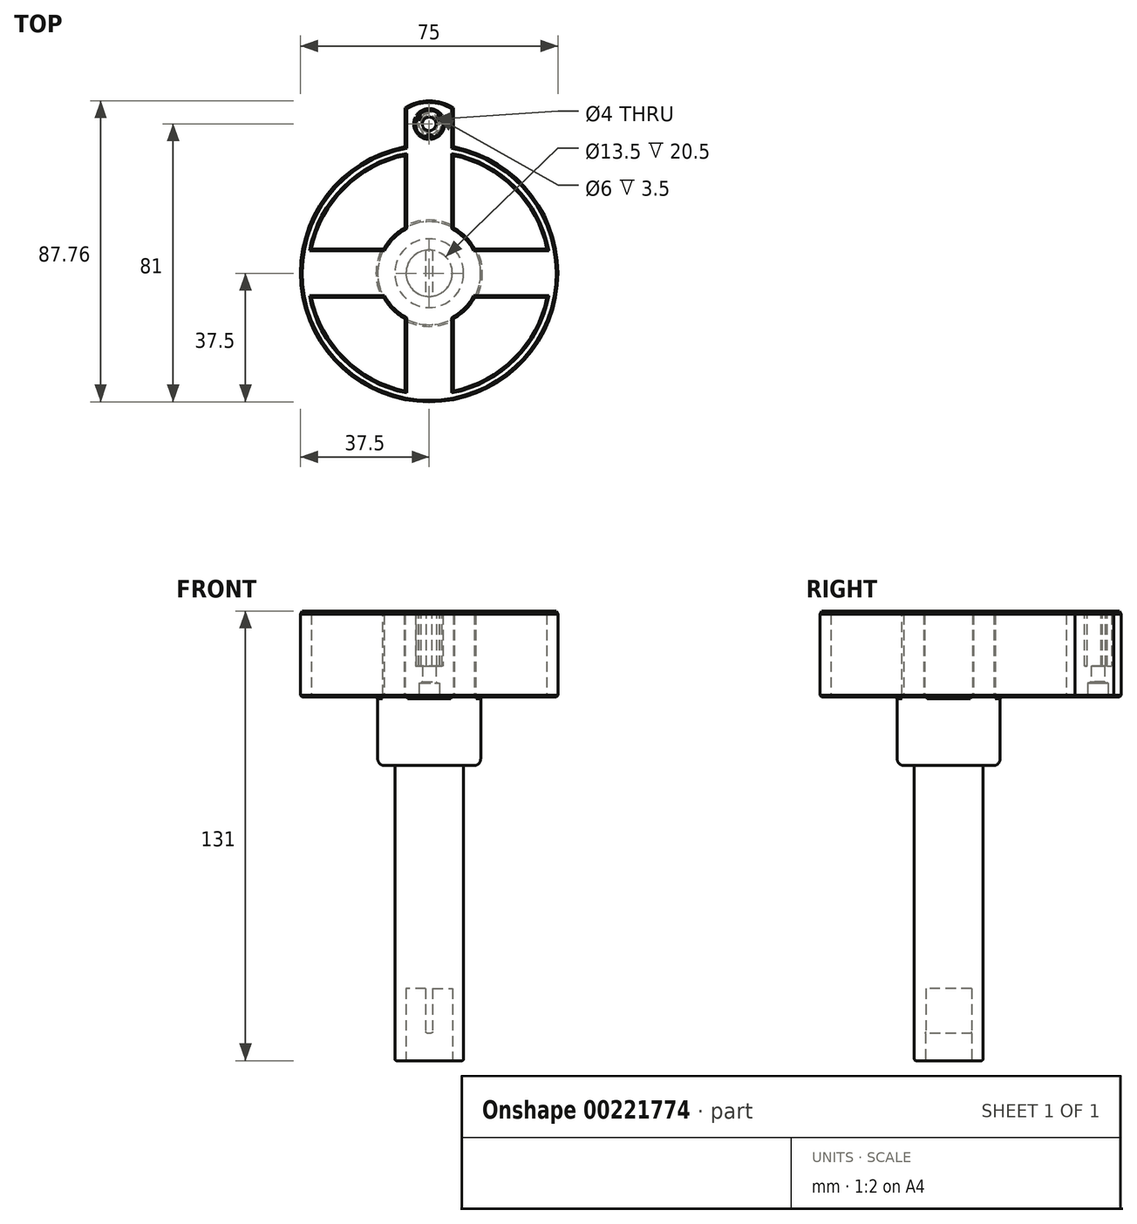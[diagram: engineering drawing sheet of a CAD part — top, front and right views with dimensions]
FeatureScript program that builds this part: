
annotation { "Feature Type Name" : "Feature", "Feature Type Description" : "" }
export const myFeature = defineFeature(function(context is Context, id is Id, definition is map)
    precondition{}
    {
        {
            var Q0;
            Q0=qCreatedBy(makeId("Top.planeOp"),FACE);
            var sketch = newSketch(context, id + "F0", { "sketchPlane" : qUnion([Q0])});
            skCircle(sketch, "E0", {"center": v(0, 0) * mm, "radius": 6.75 * mm});
            skCircle(sketch, "E1", {"center": v(0, 0) * mm, "radius": 10 * mm});
            skSolve(sketch);
        }
        {
            var Q0;
            Q0 = qSketchRegion(id + "F0", true);
            extrude(context, id + "F1", {"entities" : qUnion([Q0]), "depth" : 8 * mm});
        }
        {
            var Q0;
            Q0=makeQuery(id+"F1.opExtrude","CAP_FACE",FACE,{"disambiguationData":[OSD([sQuery(id+"F0.wireOp",EDGE,"E0"),sQuery(id+"F0.wireOp",EDGE,"E1")])],"isStart":false});
            var sketch = newSketch(context, id + "F2", { "sketchPlane" : qUnion([Q0])});
            skArc(sketch, "E2", {"start": v(-1, 6.68) * mm, "mid": v(-6.75, 0) * mm, "end": v(-1, -6.68) * mm});
            skCircle(sketch, "E3", {"center": v(0, 0) * mm, "radius": 10 * mm});
            skLineSegment(sketch, "E4", {"start": v(-1, 6.68) * mm, "end": v(-1, -6.68) * mm});
            skLineSegment(sketch, "E5", {"start": v(1, 6.68) * mm, "end": v(1, -6.68) * mm});
            skArc(sketch, "E6.trimOffspring", {"start": v(1, -6.68) * mm, "mid": v(6.75, 0) * mm, "end": v(1, 6.68) * mm});
            skSolve(sketch);
        }
        {
            var Q0;
            Q0 = qSketchRegion(id + "F2", true);
            extrude(context, id + "F3", {"entities" : qUnion([Q0]), "operationType" : NewBodyOperationType.ADD, "depth" : 13 * mm});
        }
        {
            var Q0;
            Q0=makeQuery(id+"F3.opExtrude","CAP_FACE",FACE,{"disambiguationData":[OSD([sQuery(id+"F2.wireOp",EDGE,"E2"),sQuery(id+"F2.wireOp",EDGE,"E3"),sQuery(id+"F2.wireOp",EDGE,"E4"),sQuery(id+"F2.wireOp",EDGE,"E5"),sQuery(id+"F2.wireOp",EDGE,"E6.trimOffspring")])],"isStart":false});
            var sketch = newSketch(context, id + "F4", { "sketchPlane" : qUnion([Q0])});
            skCircle(sketch, "E7", {"center": v(0, 0) * mm, "radius": 10 * mm});
            skSolve(sketch);
        }
        {
            var Q0;
            Q0 = qSketchRegion(id + "F4", true);
            extrude(context, id + "F5", {"entities" : qUnion([Q0]), "operationType" : NewBodyOperationType.ADD, "depth" : 65 * mm});
        }
        {
            var Q0;
            Q0=makeQuery(id+"F5.opExtrude","CAP_FACE",FACE,{"disambiguationData":[OSD([sQuery(id+"F4.wireOp",EDGE,"E7")])],"isStart":false});
            var sketch = newSketch(context, id + "F6", { "sketchPlane" : qUnion([Q0])});
            skCircle(sketch, "E8", {"center": v(0, 0) * mm, "radius": 15 * mm});
            skSolve(sketch);
        }
        {
            var Q0;
            Q0 = qSketchRegion(id + "F6", true);
            extrude(context, id + "F7", {"entities" : qUnion([Q0]), "operationType" : NewBodyOperationType.ADD, "depth" : 20 * mm});
        }
        {
            var Q0;
            Q0=makeQuery(id+"F7.opExtrude","CAP_FACE",FACE,{"disambiguationData":[OSD([sQuery(id+"F6.wireOp",EDGE,"E8")])],"isStart":false});
            var sketch = newSketch(context, id + "F8", { "sketchPlane" : qUnion([Q0])});
            skArc(sketch, "E9", {"start": v(-7, 13.27) * mm, "mid": v(-10.6, 10.6) * mm, "end": v(-13.27, 7) * mm});
            skArc(sketch, "E10", {"start": v(-7, 34.3) * mm, "mid": v(-24.75, 24.75) * mm, "end": v(-34.3, 7) * mm});
            skCircle(sketch, "E11", {"center": v(0, 0) * mm, "radius": 37.5 * mm});
            skLineSegment(sketch, "E12", {"start": v(7, 13.27) * mm, "end": v(7, 34.3) * mm});
            skLineSegment(sketch, "E13", {"start": v(-7, 13.27) * mm, "end": v(-7, 34.3) * mm});
            skLineSegment(sketch, "E14", {"start": v(13.27, 7) * mm, "end": v(34.3, 7) * mm});
            skLineSegment(sketch, "E15", {"start": v(13.27, -7) * mm, "end": v(34.3, -7) * mm});
            skArc(sketch, "E16.trimOffspring", {"start": v(34.3, 7) * mm, "mid": v(24.75, 24.75) * mm, "end": v(7, 34.3) * mm});
            skArc(sketch, "E17.trimOffspring", {"start": v(13.27, 7) * mm, "mid": v(10.6, 10.6) * mm, "end": v(7, 13.27) * mm});
            skLineSegment(sketch, "E18", {"start": v(-13.27, 7) * mm, "end": v(-34.3, 7) * mm});
            skLineSegment(sketch, "E19", {"start": v(-13.27, -7) * mm, "end": v(-34.3, -7) * mm});
            skArc(sketch, "E20.trimOffspring", {"start": v(-34.3, -7) * mm, "mid": v(-24.75, -24.75) * mm, "end": v(-7, -34.3) * mm});
            skArc(sketch, "E21.trimOffspring", {"start": v(-13.27, -7) * mm, "mid": v(-10.6, -10.6) * mm, "end": v(-7, -13.27) * mm});
            skLineSegment(sketch, "E22", {"start": v(-7, -13.27) * mm, "end": v(-7, -34.3) * mm});
            skLineSegment(sketch, "E23", {"start": v(7, -13.27) * mm, "end": v(7, -34.3) * mm});
            skArc(sketch, "E24.trimOffspring", {"start": v(7, -13.27) * mm, "mid": v(10.6, -10.6) * mm, "end": v(13.27, -7) * mm});
            skArc(sketch, "E25.trimOffspring", {"start": v(7, -34.3) * mm, "mid": v(24.75, -24.75) * mm, "end": v(34.3, -7) * mm});
            skLineSegment(sketch, "E26", {"start": v(-7, 36.84) * mm, "end": v(-7, 48.16) * mm});
            skLineSegment(sketch, "E27", {"start": v(7, 48.16) * mm, "end": v(7, 36.84) * mm});
            skArc(sketch, "E28", {"start": v(7, 48.16) * mm, "mid": v(0, 50.26) * mm, "end": v(-7, 48.16) * mm});
            skCircle(sketch, "E29", {"center": v(0, 43.5) * mm, "radius": 4 * mm});
            skSolve(sketch);
        }
        {
            var Q0;
            Q0 = qSketchRegion(id + "F8", true);
            extrude(context, id + "F9", {"entities" : qUnion([Q0]), "operationType" : NewBodyOperationType.ADD, "depth" : 25 * mm});
        }
        {
            var Q0;
            Q0=makeQuery(id+"F3.opExtrude","CAP_EDGE",EDGE,{"disambiguationData":[OSD([sQuery(id+"F2.wireOp",EDGE,"E5")])],"isStart":true});
            var Q1;
            Q1=makeQuery(id+"F3.opExtrude","CAP_EDGE",EDGE,{"disambiguationData":[OSD([sQuery(id+"F2.wireOp",EDGE,"E4")])],"isStart":true});
            fillet(context, id + "F10", {"entities" : qUnion([Q0, Q1]), "radius" : .5 * mm, "tangentPropagation" : true, "allowEdgeOverflow" : false});
        }
        {
            var Q0;
            Q0=makeQuery(id+"F9.opExtrude","CAP_FACE",FACE,{"disambiguationData":[OSD([sQuery(id+"F8.wireOp",EDGE,"E9"),sQuery(id+"F8.wireOp",EDGE,"E10"),sQuery(id+"F8.wireOp",EDGE,"E11"),sQuery(id+"F8.wireOp",EDGE,"E12"),sQuery(id+"F8.wireOp",EDGE,"E13"),sQuery(id+"F8.wireOp",EDGE,"E14"),sQuery(id+"F8.wireOp",EDGE,"E15"),sQuery(id+"F8.wireOp",EDGE,"E16.trimOffspring"),sQuery(id+"F8.wireOp",EDGE,"E17.trimOffspring"),sQuery(id+"F8.wireOp",EDGE,"E18"),sQuery(id+"F8.wireOp",EDGE,"E19"),sQuery(id+"F8.wireOp",EDGE,"E20.trimOffspring"),sQuery(id+"F8.wireOp",EDGE,"E21.trimOffspring"),sQuery(id+"F8.wireOp",EDGE,"E22"),sQuery(id+"F8.wireOp",EDGE,"E23"),sQuery(id+"F8.wireOp",EDGE,"E24.trimOffspring"),sQuery(id+"F8.wireOp",EDGE,"E25.trimOffspring"),sQuery(id+"F8.wireOp",EDGE,"E26"),sQuery(id+"F8.wireOp",EDGE,"E27"),sQuery(id+"F8.wireOp",EDGE,"E28"),sQuery(id+"F8.wireOp",EDGE,"E29")])],"isStart":true});
            var sketch = newSketch(context, id + "F11", { "sketchPlane" : qUnion([Q0])});
            skCircle(sketch, "E30", {"center": v(0, -43.5) * mm, "radius": 4 * mm});
            skCircle(sketch, "E31", {"center": v(0, -43.5) * mm, "radius": 2 * mm});
            skSolve(sketch);
        }
        {
            var Q0;
            Q0 = qSketchRegion(id + "F11", true);
            extrude(context, id + "F12", {"entities" : qUnion([Q0]), "operationType" : NewBodyOperationType.ADD, "oppositeDirection" : true, "depth" : 9 * mm});
        }
        {
            var Q0;
            Q0=makeQuery(id+"F12.boolean.opBoolean","MERGE",FACE,{"derivedFrom":[makeQuery(id+"F9.opExtrude","CAP_FACE",FACE,{"disambiguationData":[OSD([sQuery(id+"F8.wireOp",EDGE,"E9"),sQuery(id+"F8.wireOp",EDGE,"E10"),sQuery(id+"F8.wireOp",EDGE,"E11"),sQuery(id+"F8.wireOp",EDGE,"E12"),sQuery(id+"F8.wireOp",EDGE,"E13"),sQuery(id+"F8.wireOp",EDGE,"E14"),sQuery(id+"F8.wireOp",EDGE,"E15"),sQuery(id+"F8.wireOp",EDGE,"E16.trimOffspring"),sQuery(id+"F8.wireOp",EDGE,"E17.trimOffspring"),sQuery(id+"F8.wireOp",EDGE,"E18"),sQuery(id+"F8.wireOp",EDGE,"E19"),sQuery(id+"F8.wireOp",EDGE,"E20.trimOffspring"),sQuery(id+"F8.wireOp",EDGE,"E21.trimOffspring"),sQuery(id+"F8.wireOp",EDGE,"E22"),sQuery(id+"F8.wireOp",EDGE,"E23"),sQuery(id+"F8.wireOp",EDGE,"E24.trimOffspring"),sQuery(id+"F8.wireOp",EDGE,"E25.trimOffspring"),sQuery(id+"F8.wireOp",EDGE,"E26"),sQuery(id+"F8.wireOp",EDGE,"E27"),sQuery(id+"F8.wireOp",EDGE,"E28"),sQuery(id+"F8.wireOp",EDGE,"E29")])],"isStart":true}),makeQuery(id+"F12.opExtrude","CAP_FACE",FACE,{"disambiguationData":[OSD([sQuery(id+"F11.wireOp",EDGE,"E30"),sQuery(id+"F11.wireOp",EDGE,"E31")])],"isStart":true})]});
            var sketch = newSketch(context, id + "F13", { "sketchPlane" : qUnion([Q0])});
            skCircle(sketch, "E32", {"center": v(0, -43.5) * mm, "radius": 3 * mm});
            skSolve(sketch);
        }
        {
            var Q0;
            Q0 = qSketchRegion(id + "F13", true);
            extrude(context, id + "F14", {"entities" : qUnion([Q0]), "operationType" : NewBodyOperationType.REMOVE, "oppositeDirection" : true, "depth" : 4 * mm});
        }
        {
            var Q0;
            Q0=makeQuery(id+"F9.opExtrude","CAP_FACE",FACE,{"disambiguationData":[OSD([sQuery(id+"F8.wireOp",EDGE,"E9"),sQuery(id+"F8.wireOp",EDGE,"E10"),sQuery(id+"F8.wireOp",EDGE,"E11"),sQuery(id+"F8.wireOp",EDGE,"E12"),sQuery(id+"F8.wireOp",EDGE,"E13"),sQuery(id+"F8.wireOp",EDGE,"E14"),sQuery(id+"F8.wireOp",EDGE,"E15"),sQuery(id+"F8.wireOp",EDGE,"E16.trimOffspring"),sQuery(id+"F8.wireOp",EDGE,"E17.trimOffspring"),sQuery(id+"F8.wireOp",EDGE,"E18"),sQuery(id+"F8.wireOp",EDGE,"E19"),sQuery(id+"F8.wireOp",EDGE,"E20.trimOffspring"),sQuery(id+"F8.wireOp",EDGE,"E21.trimOffspring"),sQuery(id+"F8.wireOp",EDGE,"E22"),sQuery(id+"F8.wireOp",EDGE,"E23"),sQuery(id+"F8.wireOp",EDGE,"E24.trimOffspring"),sQuery(id+"F8.wireOp",EDGE,"E25.trimOffspring"),sQuery(id+"F8.wireOp",EDGE,"E26"),sQuery(id+"F8.wireOp",EDGE,"E27"),sQuery(id+"F8.wireOp",EDGE,"E28"),sQuery(id+"F8.wireOp",EDGE,"E29")])],"isStart":false});
            var sketch = newSketch(context, id + "F15", { "sketchPlane" : qUnion([Q0])});
            skLineSegment(sketch, "E33", {"start": v(-0.8, 39.58) * mm, "end": v(-0.8, 40.38) * mm});
            skLineSegment(sketch, "E34", {"start": v(-0.8, 40.38) * mm, "end": v(0.8, 40.38) * mm});
            skLineSegment(sketch, "E35", {"start": v(0.8, 40.38) * mm, "end": v(0.8, 39.58) * mm});
            skArc(sketch, "E36", {"start": v(-0.8, 39.58) * mm, "mid": v(0, 39.5) * mm, "end": v(0.8, 39.58) * mm});
            skLineSegment(sketch, "E37.1.0", {"start": v(3.8, 44.77) * mm, "end": v(3.1, 44.37) * mm});
            skArc(sketch, "E37.1.1", {"start": v(3.8, 44.77) * mm, "mid": v(3.46, 45.5) * mm, "end": v(3, 46.15) * mm});
            skLineSegment(sketch, "E37.1.2", {"start": v(2.3, 45.75) * mm, "end": v(3, 46.15) * mm});
            skLineSegment(sketch, "E37.1.3", {"start": v(3.1, 44.37) * mm, "end": v(2.3, 45.75) * mm});
            skLineSegment(sketch, "E37.2.0", {"start": v(-3, 46.15) * mm, "end": v(-2.3, 45.75) * mm});
            skArc(sketch, "E37.2.1", {"start": v(-3, 46.15) * mm, "mid": v(-3.46, 45.5) * mm, "end": v(-3.8, 44.77) * mm});
            skLineSegment(sketch, "E37.2.2", {"start": v(-3.1, 44.37) * mm, "end": v(-3.8, 44.77) * mm});
            skLineSegment(sketch, "E37.2.3", {"start": v(-2.3, 45.75) * mm, "end": v(-3.1, 44.37) * mm});
            skSolve(sketch);
        }
        {
            var Q0;
            Q0 = qSketchRegion(id + "F15", true);
            extrude(context, id + "F16", {"entities" : qUnion([Q0]), "operationType" : NewBodyOperationType.ADD, "oppositeDirection" : true, "depth" : 16 * mm});
        }
        {
            var Q0;
            Q0=makeQuery(id+"F16.boolean.opBoolean","MERGE",FACE,{"derivedFrom":[makeQuery(id+"F9.opExtrude","CAP_FACE",FACE,{"disambiguationData":[OSD([sQuery(id+"F8.wireOp",EDGE,"E9"),sQuery(id+"F8.wireOp",EDGE,"E10"),sQuery(id+"F8.wireOp",EDGE,"E11"),sQuery(id+"F8.wireOp",EDGE,"E12"),sQuery(id+"F8.wireOp",EDGE,"E13"),sQuery(id+"F8.wireOp",EDGE,"E14"),sQuery(id+"F8.wireOp",EDGE,"E15"),sQuery(id+"F8.wireOp",EDGE,"E16.trimOffspring"),sQuery(id+"F8.wireOp",EDGE,"E17.trimOffspring"),sQuery(id+"F8.wireOp",EDGE,"E18"),sQuery(id+"F8.wireOp",EDGE,"E19"),sQuery(id+"F8.wireOp",EDGE,"E20.trimOffspring"),sQuery(id+"F8.wireOp",EDGE,"E21.trimOffspring"),sQuery(id+"F8.wireOp",EDGE,"E22"),sQuery(id+"F8.wireOp",EDGE,"E23"),sQuery(id+"F8.wireOp",EDGE,"E24.trimOffspring"),sQuery(id+"F8.wireOp",EDGE,"E25.trimOffspring"),sQuery(id+"F8.wireOp",EDGE,"E26"),sQuery(id+"F8.wireOp",EDGE,"E27"),sQuery(id+"F8.wireOp",EDGE,"E28"),sQuery(id+"F8.wireOp",EDGE,"E29")])],"isStart":false}),makeQuery(id+"F16.opExtrude","CAP_FACE",FACE,{"disambiguationData":[OSD([sQuery(id+"F15.wireOp",EDGE,"E33"),sQuery(id+"F15.wireOp",EDGE,"E34"),sQuery(id+"F15.wireOp",EDGE,"E35"),sQuery(id+"F15.wireOp",EDGE,"E36")])],"isStart":true}),makeQuery(id+"F16.opExtrude","CAP_FACE",FACE,{"disambiguationData":[OSD([sQuery(id+"F15.wireOp",EDGE,"E37.1.0"),sQuery(id+"F15.wireOp",EDGE,"E37.1.1"),sQuery(id+"F15.wireOp",EDGE,"E37.1.2"),sQuery(id+"F15.wireOp",EDGE,"E37.1.3")])],"isStart":true}),makeQuery(id+"F16.opExtrude","CAP_FACE",FACE,{"disambiguationData":[OSD([sQuery(id+"F15.wireOp",EDGE,"E37.2.0"),sQuery(id+"F15.wireOp",EDGE,"E37.2.1"),sQuery(id+"F15.wireOp",EDGE,"E37.2.2"),sQuery(id+"F15.wireOp",EDGE,"E37.2.3")])],"isStart":true})]});
            chamfer(context, id + "F17", {"entities" : qUnion([Q0]), "chamferType" : ChamferType.OFFSET_ANGLE, "width" : .5 * mm, "oppositeDirection" : false, "angle" : 60 * degree, "tangentPropagation" : true});
        }
        {
            var Q0;
            Q0=makeQuery(id+"F14.boolean.opBoolean","INTERSECT",EDGE,{"derivedFrom":[makeQuery(id+"F12.opExtrude","SWEPT_FACE",FACE,{"disambiguationData":[OSD([sQuery(id+"F11.wireOp",EDGE,"E31")])]}),makeQuery(id+"F14.opExtrude","CAP_FACE",FACE,{"disambiguationData":[OSD([sQuery(id+"F13.wireOp",EDGE,"E32")])],"isStart":false})]});
            var Q1;
            Q1=makeQuery(id+"F12.boolean.opBoolean","MERGE",FACE,{"derivedFrom":[makeQuery(id+"F9.opExtrude","CAP_FACE",FACE,{"disambiguationData":[OSD([sQuery(id+"F8.wireOp",EDGE,"E9"),sQuery(id+"F8.wireOp",EDGE,"E10"),sQuery(id+"F8.wireOp",EDGE,"E11"),sQuery(id+"F8.wireOp",EDGE,"E12"),sQuery(id+"F8.wireOp",EDGE,"E13"),sQuery(id+"F8.wireOp",EDGE,"E14"),sQuery(id+"F8.wireOp",EDGE,"E15"),sQuery(id+"F8.wireOp",EDGE,"E16.trimOffspring"),sQuery(id+"F8.wireOp",EDGE,"E17.trimOffspring"),sQuery(id+"F8.wireOp",EDGE,"E18"),sQuery(id+"F8.wireOp",EDGE,"E19"),sQuery(id+"F8.wireOp",EDGE,"E20.trimOffspring"),sQuery(id+"F8.wireOp",EDGE,"E21.trimOffspring"),sQuery(id+"F8.wireOp",EDGE,"E22"),sQuery(id+"F8.wireOp",EDGE,"E23"),sQuery(id+"F8.wireOp",EDGE,"E24.trimOffspring"),sQuery(id+"F8.wireOp",EDGE,"E25.trimOffspring"),sQuery(id+"F8.wireOp",EDGE,"E26"),sQuery(id+"F8.wireOp",EDGE,"E27"),sQuery(id+"F8.wireOp",EDGE,"E28"),sQuery(id+"F8.wireOp",EDGE,"E29")])],"isStart":true}),makeQuery(id+"F12.opExtrude","CAP_FACE",FACE,{"disambiguationData":[OSD([sQuery(id+"F11.wireOp",EDGE,"E30"),sQuery(id+"F11.wireOp",EDGE,"E31")])],"isStart":true})]});
            chamfer(context, id + "F18", {"entities" : qUnion([Q0, Q1]), "width" : .5 * mm, "tangentPropagation" : true});
        }
        {
            var Q0;
            Q0=makeQuery(id+"F7.opExtrude","CAP_EDGE",EDGE,{"disambiguationData":[OSD([sQuery(id+"F6.wireOp",EDGE,"E8")])],"isStart":true});
            var Q1;
            Q1=makeQuery(id+"F5.opExtrude","CAP_EDGE",EDGE,{"disambiguationData":[OSD([sQuery(id+"F4.wireOp",EDGE,"E7")])],"isStart":false});
            fillet(context, id + "F19", {"entities" : qUnion([Q0, Q1]), "radius" : 2 * mm, "tangentPropagation" : true, "allowEdgeOverflow" : false});
        }
        {
            var Q0;
            Q0=makeQuery(id+"F1.opExtrude","CAP_EDGE",EDGE,{"disambiguationData":[OSD([sQuery(id+"F0.wireOp",EDGE,"E0")])],"isStart":true});
            var Q1;
            Q1=makeQuery(id+"F1.opExtrude","CAP_EDGE",EDGE,{"disambiguationData":[OSD([sQuery(id+"F0.wireOp",EDGE,"E1")])],"isStart":true});
            fillet(context, id + "F20", {"entities" : qUnion([Q0, Q1]), "radius" : .5 * mm, "tangentPropagation" : true, "allowEdgeOverflow" : false});
        }
    });
